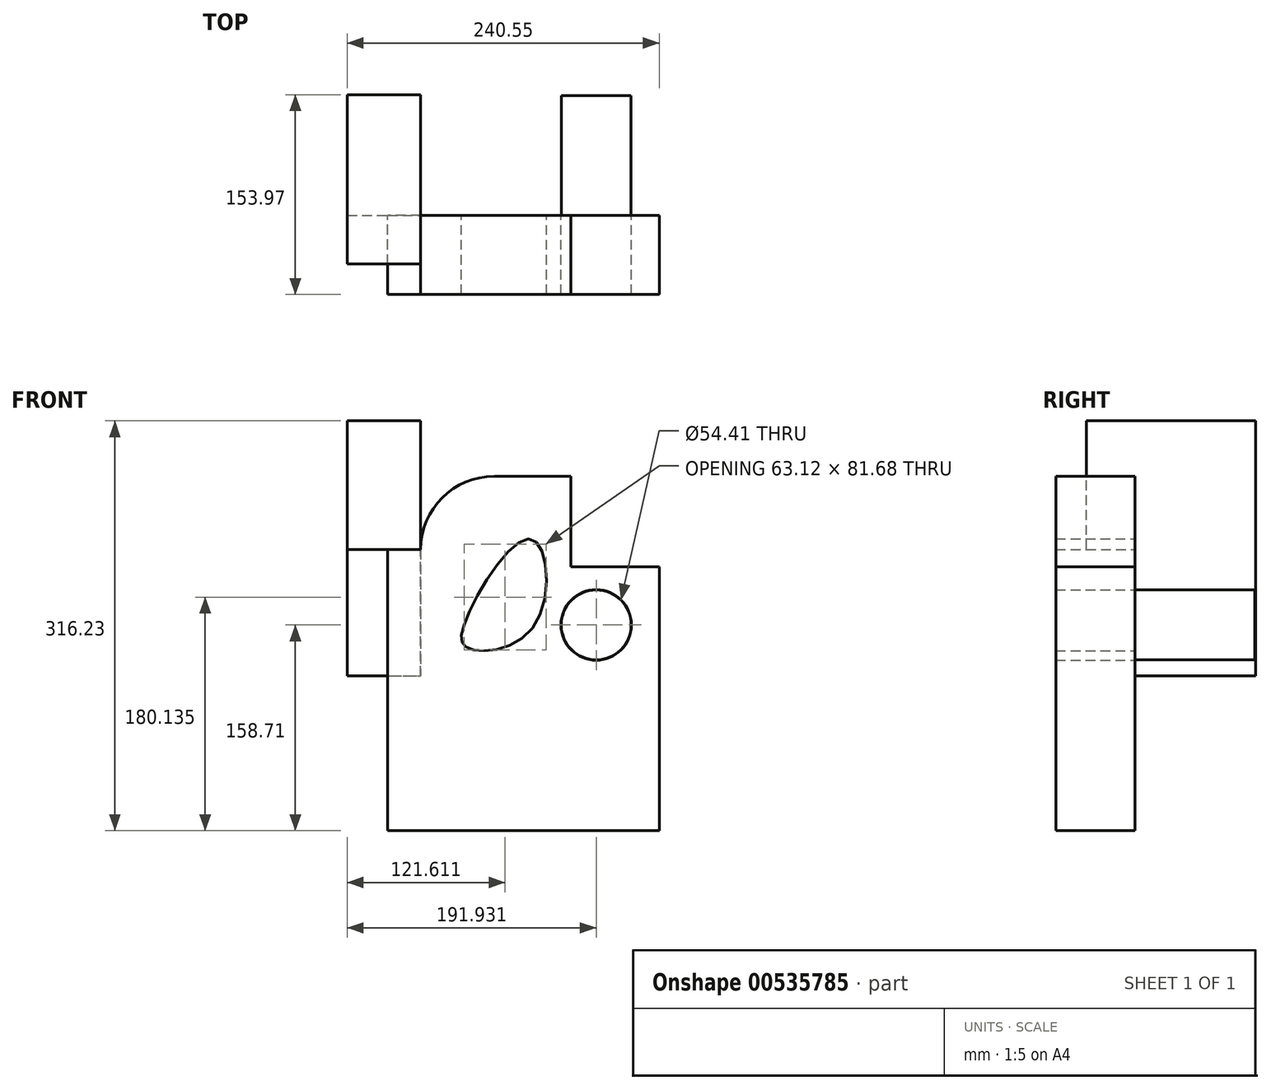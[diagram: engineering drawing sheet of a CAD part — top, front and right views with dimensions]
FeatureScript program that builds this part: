
annotation { "Feature Type Name" : "Feature", "Feature Type Description" : "" }
export const myFeature = defineFeature(function(context is Context, id is Id, definition is map)
    precondition{}
    {
        {
            var Q0;
            Q0=qCreatedBy(makeId("Front.planeOp"),FACE);
            var sketch = newSketch(context, id + "F0", { "sketchPlane" : qUnion([Q0])});
            skLineSegment(sketch, "E0", {"start": v(-62.78, -70.33) * mm, "end": v(-62.78, 114.72) * mm});
            skLineSegment(sketch, "E1", {"start": v(-62.78, 114.72) * mm, "end": v(53.05, 114.72) * mm});
            skLineSegment(sketch, "E2", {"start": v(53.05, 114.72) * mm, "end": v(53.05, 44.71) * mm});
            skLineSegment(sketch, "E3", {"start": v(53.05, 44.71) * mm, "end": v(121.12, 44.71) * mm});
            skLineSegment(sketch, "E4", {"start": v(121.12, 44.71) * mm, "end": v(121.12, -70.33) * mm});
            skLineSegment(sketch, "E5", {"start": v(121.12, -70.33) * mm, "end": v(-62.78, -70.33) * mm});
            skCircle(sketch, "E6", {"center": v(72.5, 0) * mm, "radius": 27.2 * mm});
            skFitSpline(sketch, "E7", {"points": [v(-29.38, 0) * mm, v(21.98, 66.26) * mm, v(25.15, 0) * mm, v(-25.58, -18.32) * mm, v(-29.38, 0) * mm]});
            skSolve(sketch);
        }
        {
            var Q0;
            Q0 = qSketchRegion(id + "F0", true);
            extrude(context, id + "F1", {"entities" : qUnion([Q0]), "depth" : 60.9 * mm, "offsetDistance" : 25.4 * mm});
        }
        {
            var Q0;
            Q0=makeQuery(id+"F1.opExtrude","SWEPT_EDGE",EDGE,{"disambiguationData":[OSD([sQuery(id+"F0.wireOp",EDGE,"E0"),sQuery(id+"F0.wireOp",EDGE,"E1")])]});
            fillet(context, id + "F2", {"entities" : qUnion([Q0]), "radius" : 56.68 * mm, "tangentPropagation" : true, "allowEdgeOverflow" : false});
        }
        {
            var Q0;
            Q0=makeQuery(id+"F1.opExtrude","CAP_FACE",FACE,{"disambiguationData":[OSD([sQuery(id+"F0.wireOp",EDGE,"E0"),sQuery(id+"F0.wireOp",EDGE,"E1"),sQuery(id+"F0.wireOp",EDGE,"E2"),sQuery(id+"F0.wireOp",EDGE,"E3"),sQuery(id+"F0.wireOp",EDGE,"E4"),sQuery(id+"F0.wireOp",EDGE,"E5"),sQuery(id+"F0.wireOp",EDGE,"E6"),sQuery(id+"F0.wireOp",EDGE,"E7")])],"isStart":true});
            var sketch = newSketch(context, id + "F3", { "sketchPlane" : qUnion([Q0])});
            skCircle(sketch, "E8", {"center": v(-72.5, 0) * mm, "radius": 26.92 * mm});
            skSolve(sketch);
        }
        {
            var Q0;
            Q0=makeQuery(id+"F3.imprint","IMPRINT",FACE,{"disambiguationData":[TD([[makeQuery(id+"F3.imprint","IMPRINT",EDGE,{"derivedFrom":sQuery(id+"F3.wireOp",EDGE,"E8")}),1.0]])]});
            extrude(context, id + "F4", {"entities" : qUnion([Q0]), "depth" : 188.12 * mm, "offsetDistance" : 25.4 * mm});
        }
        {
            var Q0;
            Q0=makeQuery(id+"F4.opExtrude","CAP_FACE",FACE,{"disambiguationData":[OSD([sQuery(id+"F3.wireOp",EDGE,"E8")])],"isStart":false});
            extrude(context, id + "F5", {"entities" : qUnion([Q0]), "operationType" : NewBodyOperationType.ADD, "oppositeDirection" : true, "depth" : 143.78 * mm, "offsetDistance" : 25.4 * mm});
        }
        {
            var Q0;
            Q0=makeQuery(id+"F1.opExtrude","SWEPT_FACE",FACE,{"disambiguationData":[OSD([sQuery(id+"F0.wireOp",EDGE,"E0")])]});
            var sketch = newSketch(context, id + "F6", { "sketchPlane" : qUnion([Q0])});
            skLineSegment(sketch, "E9.bottom", {"start": v(37.48, -39.22) * mm, "end": v(-93.08, -39.22) * mm});
            skLineSegment(sketch, "E9.top", {"start": v(37.48, 157.52) * mm, "end": v(-93.08, 157.52) * mm});
            skLineSegment(sketch, "E9.left", {"start": v(37.48, -39.22) * mm, "end": v(37.48, 157.52) * mm});
            skLineSegment(sketch, "E9.right", {"start": v(-93.08, -39.22) * mm, "end": v(-93.08, 157.52) * mm});
            skSolve(sketch);
        }
        {
            var Q0;
            {var subQ2=sQuery(id+"F6.wireOp",EDGE,"E9.top");Q0=makeQuery(id+"F6.imprint","IMPRINT",FACE,{"disambiguationData":[TD([[makeQuery(id+"F6.imprint","IMPRINT",EDGE,{"derivedFrom":subQ2}),1.0]])]});}
            extrude(context, id + "F7", {"entities" : qUnion([Q0]), "operationType" : NewBodyOperationType.ADD, "depth" : 56.65 * mm, "offsetDistance" : 25.4 * mm});
        }
        {
            var Q0;
            Q0=makeQuery(id+"F1.opExtrude","SWEPT_FACE",FACE,{"disambiguationData":[OSD([sQuery(id+"F0.wireOp",EDGE,"E0")])]});
            extrude(context, id + "F8", {"entities" : qUnion([Q0]), "operationType" : NewBodyOperationType.ADD, "depth" : 25.4 * mm, "offsetDistance" : 25.4 * mm});
        }
        {
            var Q0;
            {var subQ0=sQuery(id+"F0.wireOp",EDGE,"E5");Q0=makeQuery(id+"F8.boolean.opBoolean","MERGE",FACE,{"derivedFrom":[makeQuery(id+"F1.opExtrude","SWEPT_FACE",FACE,{"disambiguationData":[OSD([subQ0])]}),makeQuery(id+"F8.opExtrude","SWEPT_FACE",FACE,{"disambiguationData":[OSD([sQuery(id+"F0.wireOp",EDGE,"E0"),subQ0])]})]});}
            extrude(context, id + "F9", {"entities" : qUnion([Q0]), "operationType" : NewBodyOperationType.ADD, "depth" : 88.38 * mm, "offsetDistance" : 25.4 * mm});
        }
        {
            var Q0;
            Q0=makeQuery(id+"F4.opExtrude","CAP_FACE",FACE,{"disambiguationData":[OSD([sQuery(id+"F3.wireOp",EDGE,"E8")])],"isStart":false});
            extrude(context, id + "F10", {"entities" : qUnion([Q0]), "operationType" : NewBodyOperationType.REMOVE, "oppositeDirection" : true, "depth" : 95.6 * mm, "offsetDistance" : 25.4 * mm});
        }
    });
